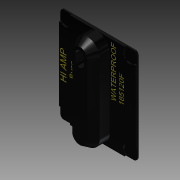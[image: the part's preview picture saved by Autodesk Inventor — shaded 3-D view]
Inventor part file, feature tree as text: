
AUTODESK INVENTOR PART (.ipt)
format: ipt  version: 2013 (Build 170138000, 138)  size: 675,328 bytes
history: native  units: mm (DEFAULTED — no unit token found)
features: sketch x6, extrude x4, plane x3, mirror x2, emboss x2, chamfer x1, reference x1
ambient origin geometry x8: Origin, YZ Plane, XZ Plane, XY Plane, X Axis, Y Axis, Z Axis, Center Point
bodies: Solid1 (feature_tree)
feature tree (19):
  extrude  "Extrusion1"  Depth=6.35mm
  extrude  "Extrusion2"  Depth=3.81mm
  chamfer  "Chamfer2"  Distance=8.89mm
  extrude  "Extrusion3"  Depth=0.762mm
  plane  "Work Plane1"
  plane  "Work Plane2"
  extrude  "Extrusion5"  Depth=0.762mm TaperAngle=0.0deg
  mirror  "Mirror3"
  mirror  "Mirror4"
  emboss  "Emboss1"
  emboss  "Emboss2"
  plane  "Work Plane3"
  sketch  "Sketch1"  dims[d0=1.524mm d1=0.0mm d2=6.35mm]
  reference  "Reference1"
  sketch  "Sketch2"  dims[d3=8.89mm d4=0.0mm d7=3.81mm d8=2.54mm]
  sketch  "Sketch3"  dims[d10=2.159mm]
  sketch  "Sketch5"  dims[d11=7.62mm d12=8.89mm d13=0.0mm]
  sketch  "Sketch6"  dims[d17=6.35mm d18=0.762mm]
  sketch  "Sketch7"  dims[d19=0.762mm d20=0.762mm d21=0.0mm d22=0.0508mm d23=0.0mm d24=0.0508mm d25=0.0mm d26=45.0deg]
